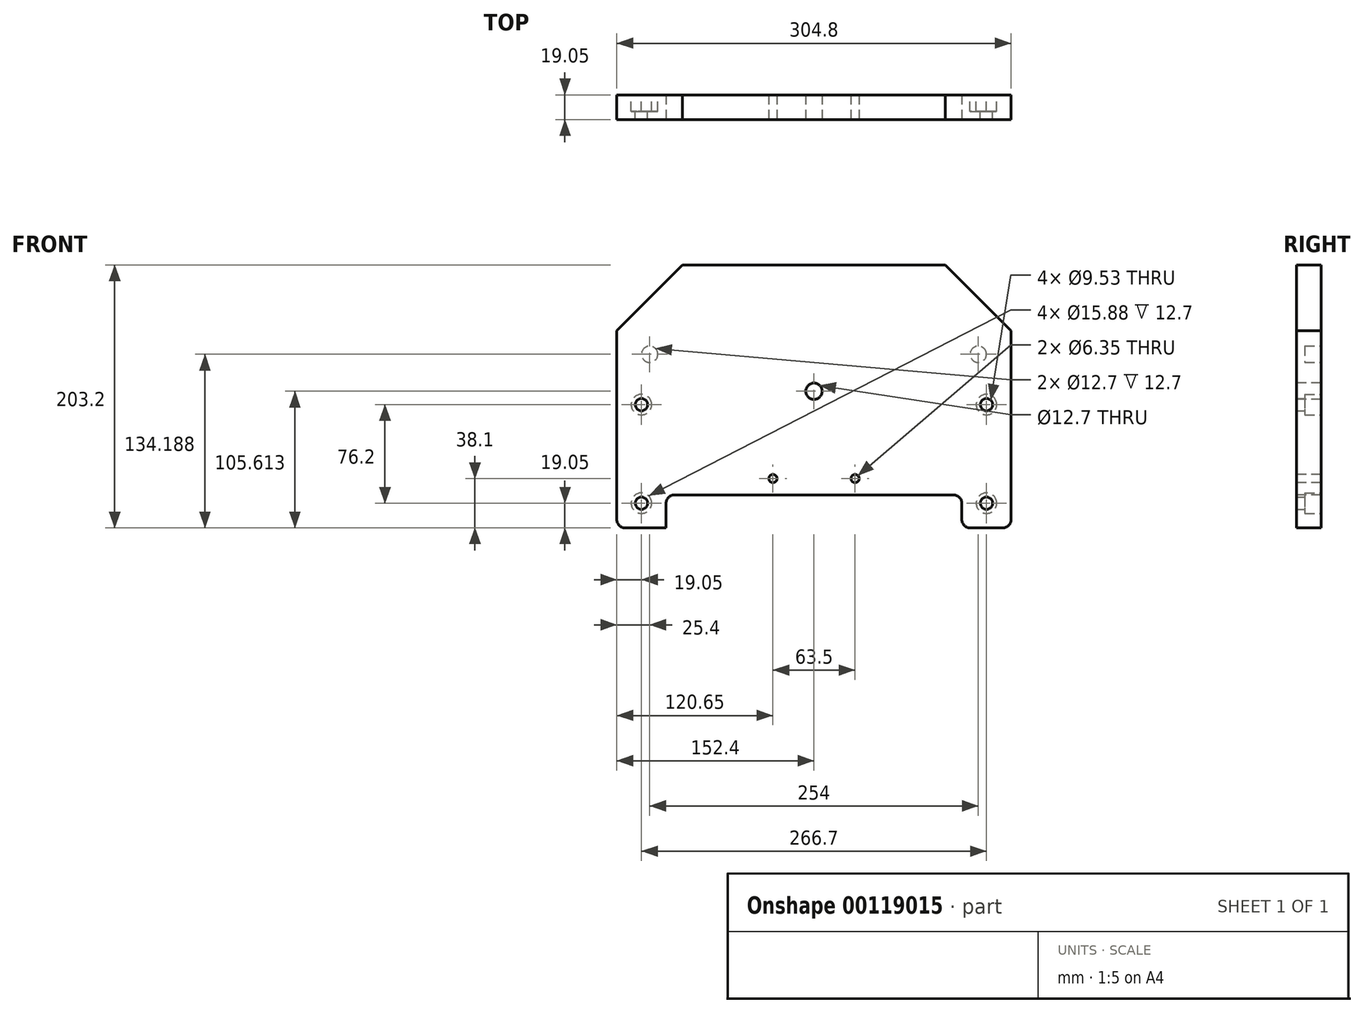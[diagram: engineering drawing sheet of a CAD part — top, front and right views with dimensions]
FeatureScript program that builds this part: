
annotation { "Feature Type Name" : "Feature", "Feature Type Description" : "" }
export const myFeature = defineFeature(function(context is Context, id is Id, definition is map)
    precondition{}
    {
        {
            var Q0;
            Q0=qCreatedBy(makeId("Front.planeOp"),FACE);
            var sketch = newSketch(context, id + "F0", { "sketchPlane" : qUnion([Q0])});
            skLineSegment(sketch, "E0.bottom", {"start": v(0, 0) * mm, "end": v(304.8, 0) * mm});
            skLineSegment(sketch, "E0.top", {"start": v(0, 203.2) * mm, "end": v(304.8, 203.2) * mm});
            skLineSegment(sketch, "E0.left", {"start": v(0, 0) * mm, "end": v(0, 203.2) * mm});
            skLineSegment(sketch, "E0.right", {"start": v(304.8, 0) * mm, "end": v(304.8, 203.2) * mm});
            skSolve(sketch);
        }
        {
            var Q0;
            Q0=makeQuery(id+"F0.imprint","IMPRINT",FACE,{"disambiguationData":[TD([[makeQuery(id+"F0.imprint","IMPRINT",EDGE,{"derivedFrom":sQuery(id+"F0.wireOp",EDGE,"E0.bottom")}),1.0]])]});
            extrude(context, id + "F1", {"entities" : qUnion([Q0]), "depth" : 19.05 * mm});
        }
        {
            var Q0;
            Q0=makeQuery(id+"F1.opExtrude","CAP_FACE",FACE,{"disambiguationData":[OSD([sQuery(id+"F0.wireOp",EDGE,"E0.bottom"),sQuery(id+"F0.wireOp",EDGE,"E0.top"),sQuery(id+"F0.wireOp",EDGE,"E0.left"),sQuery(id+"F0.wireOp",EDGE,"E0.right")])],"isStart":false});
            var sketch = newSketch(context, id + "F2", { "sketchPlane" : qUnion([Q0])});
            skLineSegment(sketch, "E1.bottom", {"start": v(38.1, 0) * mm, "end": v(266.7, 0) * mm});
            skLineSegment(sketch, "E1.top", {"start": v(38.1, 25.4) * mm, "end": v(266.7, 25.4) * mm});
            skLineSegment(sketch, "E1.left", {"start": v(38.1, 0) * mm, "end": v(38.1, 25.4) * mm});
            skLineSegment(sketch, "E1.right", {"start": v(266.7, 0) * mm, "end": v(266.7, 25.4) * mm});
            skSolve(sketch);
        }
        {
            var Q0;
            Q0 = qSketchRegion(id + "F2", true);
            extrude(context, id + "F3", {"entities" : qUnion([Q0]), "operationType" : NewBodyOperationType.REMOVE, "endBound" : BoundingType.THROUGH_ALL, "oppositeDirection" : true, "depth" : 25.4 * mm});
        }
        {
            var Q0;
            Q0=makeQuery(id+"F1.opExtrude","CAP_FACE",FACE,{"disambiguationData":[OSD([sQuery(id+"F0.wireOp",EDGE,"E0.bottom"),sQuery(id+"F0.wireOp",EDGE,"E0.top"),sQuery(id+"F0.wireOp",EDGE,"E0.left"),sQuery(id+"F0.wireOp",EDGE,"E0.right")])],"isStart":false});
            var sketch = newSketch(context, id + "F4", { "sketchPlane" : qUnion([Q0])});
            skLineSegment(sketch, "E2", {"start": v(152.4, 203.2) * mm, "end": v(152.4, 25.4) * mm, "construction": true});
            skLineSegment(sketch, "E3", {"start": v(152.4, 38.1) * mm, "end": v(120.65, 38.1) * mm, "construction": true});
            skLineSegment(sketch, "E4", {"start": v(152.4, 38.1) * mm, "end": v(184.15, 38.1) * mm, "construction": true});
            skPoint(sketch, "E5", {"position": v(120.65, 38.1) * mm});
            skPoint(sketch, "E6", {"position": v(184.15, 38.1) * mm});
            skSolve(sketch);
        }
        {
            var Q0;
            Q0=sQuery(id+"F4.wireOp",VERTEX,"E5");
            var Q1;
            Q1=sQuery(id+"F4.wireOp",VERTEX,"E6");
            var Q2;
            Q2=makeQuery(id+"F1.opExtrude","SWEPT_BODY",BODY,{"disambiguationData":[OSD([sQuery(id+"F0.wireOp",EDGE,"E0.bottom"),sQuery(id+"F0.wireOp",EDGE,"E0.top"),sQuery(id+"F0.wireOp",EDGE,"E0.left"),sQuery(id+"F0.wireOp",EDGE,"E0.right")])]});
            hole(context, id + "F5", {"style" : HoleStyle.SIMPLE, "endStyle" : HoleEndStyle.THROUGH, "holeDiameter" : 6.35 * mm, "locations" : qUnion([Q0, Q1]), "scope" : qUnion([Q2]), "isTappedThrough" : true});
        }
        {
            var Q0;
            Q0=makeQuery(id+"F3.boolean.opBoolean","COPY",EDGE,{"derivedFrom":makeQuery(id+"F3.opExtrude","SWEPT_EDGE",EDGE,{"disambiguationData":[OSD([sQuery(id+"F2.wireOp",EDGE,"E1.top"),sQuery(id+"F2.wireOp",EDGE,"E1.left")])]})});
            var Q1;
            Q1=makeQuery(id+"F3.boolean.opBoolean","COPY",EDGE,{"derivedFrom":makeQuery(id+"F3.opExtrude","SWEPT_EDGE",EDGE,{"disambiguationData":[OSD([sQuery(id+"F0.wireOp",EDGE,"E0.bottom"),sQuery(id+"F2.wireOp",EDGE,"E1.bottom"),sQuery(id+"F2.wireOp",EDGE,"E1.left")])]})});
            var Q2;
            Q2=makeQuery(id+"F1.opExtrude","SWEPT_EDGE",EDGE,{"disambiguationData":[OSD([sQuery(id+"F0.wireOp",EDGE,"E0.bottom"),sQuery(id+"F0.wireOp",EDGE,"E0.left")])]});
            var Q3;
            Q3=makeQuery(id+"F3.boolean.opBoolean","COPY",EDGE,{"derivedFrom":makeQuery(id+"F3.opExtrude","SWEPT_EDGE",EDGE,{"disambiguationData":[OSD([sQuery(id+"F2.wireOp",EDGE,"E1.top"),sQuery(id+"F2.wireOp",EDGE,"E1.right")])]})});
            var Q4;
            Q4=makeQuery(id+"F3.boolean.opBoolean","COPY",EDGE,{"derivedFrom":makeQuery(id+"F3.opExtrude","SWEPT_EDGE",EDGE,{"disambiguationData":[OSD([sQuery(id+"F0.wireOp",EDGE,"E0.bottom"),sQuery(id+"F2.wireOp",EDGE,"E1.bottom"),sQuery(id+"F2.wireOp",EDGE,"E1.right")])]})});
            var Q5;
            Q5=makeQuery(id+"F1.opExtrude","SWEPT_EDGE",EDGE,{"disambiguationData":[OSD([sQuery(id+"F0.wireOp",EDGE,"E0.bottom"),sQuery(id+"F0.wireOp",EDGE,"E0.right")])]});
            fillet(context, id + "F6", {"entities" : qUnion([Q0, Q1, Q2, Q3, Q4, Q5]), "radius" : 6.35 * mm, "tangentPropagation" : true, "allowEdgeOverflow" : false});
        }
        {
            var Q0;
            Q0=makeQuery(id+"F1.opExtrude","CAP_FACE",FACE,{"disambiguationData":[OSD([sQuery(id+"F0.wireOp",EDGE,"E0.bottom"),sQuery(id+"F0.wireOp",EDGE,"E0.top"),sQuery(id+"F0.wireOp",EDGE,"E0.left"),sQuery(id+"F0.wireOp",EDGE,"E0.right")])],"isStart":false});
            var sketch = newSketch(context, id + "F7", { "sketchPlane" : qUnion([Q0])});
            skLineSegment(sketch, "E7", {"start": v(152.4, 25.4) * mm, "end": v(152.4, 105.61) * mm, "construction": true});
            skPoint(sketch, "E8", {"position": v(152.4, 105.61) * mm});
            skSolve(sketch);
        }
        {
            var Q0;
            Q0=sQuery(id+"F7.wireOp",VERTEX,"E8");
            var Q1;
            Q1=makeQuery(id+"F1.opExtrude","SWEPT_BODY",BODY,{"disambiguationData":[OSD([sQuery(id+"F0.wireOp",EDGE,"E0.bottom"),sQuery(id+"F0.wireOp",EDGE,"E0.top"),sQuery(id+"F0.wireOp",EDGE,"E0.left"),sQuery(id+"F0.wireOp",EDGE,"E0.right")])]});
            hole(context, id + "F8", {"style" : HoleStyle.SIMPLE, "endStyle" : HoleEndStyle.THROUGH, "holeDiameter" : 12.7 * mm, "locations" : qUnion([Q0]), "scope" : qUnion([Q1]), "isTappedThrough" : true});
        }
        {
            var Q0;
            Q0=makeQuery(id+"F1.opExtrude","CAP_FACE",FACE,{"disambiguationData":[OSD([sQuery(id+"F0.wireOp",EDGE,"E0.bottom"),sQuery(id+"F0.wireOp",EDGE,"E0.top"),sQuery(id+"F0.wireOp",EDGE,"E0.left"),sQuery(id+"F0.wireOp",EDGE,"E0.right")])],"isStart":true});
            var sketch = newSketch(context, id + "F9", { "sketchPlane" : qUnion([Q0])});
            skCircle(sketch, "E9", {"center": v(-25.4, 134.19) * mm, "radius": 6.35 * mm});
            skLineSegment(sketch, "E10", {"start": v(-152.4, 105.61) * mm, "end": v(-152.4, 134.19) * mm, "construction": true});
            skCircle(sketch, "E11", {"center": v(-279.4, 134.19) * mm, "radius": 6.35 * mm});
            skLineSegment(sketch, "E12", {"start": v(-279.4, 134.19) * mm, "end": v(-152.4, 134.19) * mm, "construction": true});
            skSolve(sketch);
        }
        {
            var Q0;
            Q0 = qSketchRegion(id + "F9", true);
            extrude(context, id + "F10", {"entities" : qUnion([Q0]), "operationType" : NewBodyOperationType.REMOVE, "oppositeDirection" : true, "depth" : 12.7 * mm});
        }
        {
            var Q0;
            Q0=makeQuery(id+"F1.opExtrude","CAP_FACE",FACE,{"disambiguationData":[OSD([sQuery(id+"F0.wireOp",EDGE,"E0.bottom"),sQuery(id+"F0.wireOp",EDGE,"E0.top"),sQuery(id+"F0.wireOp",EDGE,"E0.left"),sQuery(id+"F0.wireOp",EDGE,"E0.right")])],"isStart":true});
            var sketch = newSketch(context, id + "F11", { "sketchPlane" : qUnion([Q0])});
            skPoint(sketch, "E13", {"position": v(-285.75, 19.05) * mm});
            skPoint(sketch, "E13.positionSnap0", {"position": v(-285.75, 0) * mm});
            skPoint(sketch, "E14", {"position": v(-285.75, 95.25) * mm});
            skPoint(sketch, "E15", {"position": v(-19.05, 19.05) * mm});
            skPoint(sketch, "E15.positionSnap0", {"position": v(-19.05, 0) * mm});
            skPoint(sketch, "E16", {"position": v(-19.05, 95.25) * mm});
            skSolve(sketch);
        }
        {
            var Q0;
            Q0=sQuery(id+"F11.wireOp",VERTEX,"E14");
            var Q1;
            Q1=sQuery(id+"F11.wireOp",VERTEX,"E13");
            var Q2;
            Q2=sQuery(id+"F11.wireOp",VERTEX,"E15");
            var Q3;
            Q3=sQuery(id+"F11.wireOp",VERTEX,"E16");
            var Q4;
            Q4=makeQuery(id+"F1.opExtrude","SWEPT_BODY",BODY,{"disambiguationData":[OSD([sQuery(id+"F0.wireOp",EDGE,"E0.bottom"),sQuery(id+"F0.wireOp",EDGE,"E0.top"),sQuery(id+"F0.wireOp",EDGE,"E0.left"),sQuery(id+"F0.wireOp",EDGE,"E0.right")])]});
            hole(context, id + "F12", {"style" : HoleStyle.C_BORE, "endStyle" : HoleEndStyle.THROUGH, "holeDiameter" : 9.52 * mm, "cBoreDiameter" : 15.88 * mm, "cBoreDepth" : 12.7 * mm, "locations" : qUnion([Q0, Q1, Q2, Q3]), "scope" : qUnion([Q4]), "isTappedThrough" : true});
        }
        {
            var Q0;
            Q0=makeQuery(id+"F1.opExtrude","SWEPT_EDGE",EDGE,{"disambiguationData":[OSD([sQuery(id+"F0.wireOp",EDGE,"E0.top"),sQuery(id+"F0.wireOp",EDGE,"E0.left")])]});
            var Q1;
            Q1=makeQuery(id+"F1.opExtrude","SWEPT_EDGE",EDGE,{"disambiguationData":[OSD([sQuery(id+"F0.wireOp",EDGE,"E0.top"),sQuery(id+"F0.wireOp",EDGE,"E0.right")])]});
            chamfer(context, id + "F13", {"entities" : qUnion([Q0, Q1]), "width" : 50.8 * mm});
        }
    });
